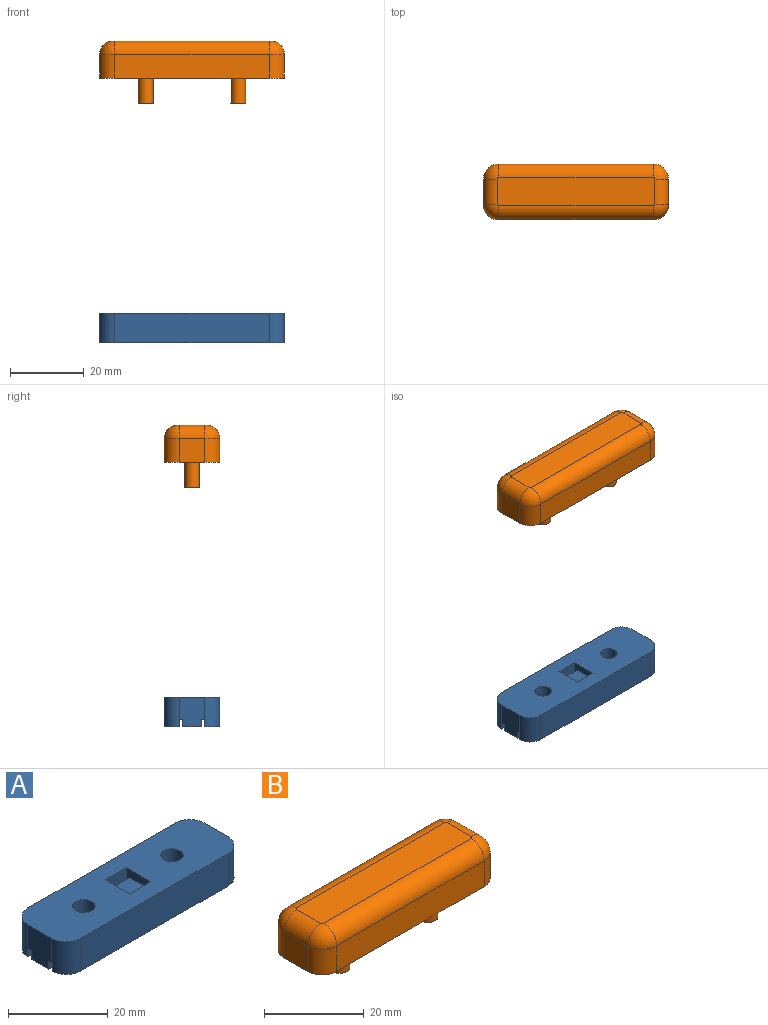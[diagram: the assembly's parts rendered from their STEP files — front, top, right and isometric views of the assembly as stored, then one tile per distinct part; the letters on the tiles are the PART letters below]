
ASSEMBLY  parts=2 mates=1
PART A: 25 faces, bbox 50x15x8 mm
  f0: plane 50x4mm, normal (0,0,-1), area 192.8mm2, adj f6,f7,f21,f22
  f1: plane 50x5mm, normal (0,0,-1), area 218.2mm2, adj f3,f10,f12,f13,f14,f15
  f2: plane 50x4mm, normal (0,0,-1), area 192.8mm2, adj f5,f8,f23,f24
  f3: plane 8x6.82mm, normal (1,0,0), area 50.9mm2, adj f1,f11,f14,f15,f19,f20,f21,f24
  f4: plane 7x6mm, normal (-1,0,0), area 22mm2, adj f7,f8,f11,f14,f15,f16,f19,f20
  f5: plane 41.82x8mm, normal (0,-1,0), area 334.6mm2, adj f2,f11,f23,f24
  f6: plane 41.82x8mm, normal (0,1,0), area 334.6mm2, adj f0,f11,f21,f22
  f7: plane 50x8mm, normal (0,-1,0), area 136mm2, adj f0,f4,f9,f11,f18,f20,f21,f22
  f8: plane 50x8mm, normal (0,1,0), area 136mm2, adj f2,f4,f9,f11,f17,f19,f23,f24
  f9: plane 7x6mm, normal (1,0,0), area 22mm2, adj f7,f8,f11,f14,f15,f16,f17,f18
  f10: plane 8x6.82mm, normal (-1,0,0), area 50.9mm2, adj f1,f11,f14,f15,f17,f18,f22,f23
  f11: plane 50x15mm, normal (0,0,1), area 661.8mm2, adj f3,f4,f5,f6,f7,f8,f9,f10
  f12: cylinder r=2.25mm len=8mm, axis (0,0,-1), area 113.1mm2, adj f1,f11
  f13: cylinder r=2.25mm len=8mm, axis (0,0,-1), area 113.1mm2, adj f1,f11
  f14: plane 50x6mm, normal (0,-1,0), area 124mm2, adj f1,f3,f4,f9,f10,f16,f17,f19
  f15: plane 50x6mm, normal (0,1,0), area 124mm2, adj f1,f3,f4,f9,f10,f16,f18,f20
  f16: plane 6x5mm, normal (0,0,1), area 30mm2, adj f4,f9,f14,f15
  f17: plane 22x1mm, normal (0,0,-1), area 22mm2, adj f8,f9,f10,f14,f23
  f18: plane 22x1mm, normal (0,0,-1), area 22mm2, adj f7,f9,f10,f15,f22
  f19: plane 22x1mm, normal (0,0,-1), area 22mm2, adj f3,f4,f8,f14,f24
  f20: plane 22x1mm, normal (0,0,-1), area 22mm2, adj f3,f4,f7,f15,f21
  f21: cylinder r=4.09mm len=8mm, axis (0,0,1), area 51.2mm2, adj f0,f3,f6,f7,f11,f20
  f22: cylinder r=4.09mm len=8mm, axis (0,0,-1), area 51.2mm2, adj f0,f6,f7,f10,f11,f18
  f23: cylinder r=4.09mm len=8mm, axis (0,0,1), area 51.2mm2, adj f2,f5,f8,f10,f11,f17
  f24: cylinder r=4.09mm len=8mm, axis (0,0,-1), area 51.2mm2, adj f2,f3,f5,f8,f11,f19
PART B: 24 faces, bbox 50x15x17 mm
  f0: plane 42.64x7.64mm, normal (0,0,1), area 325.7mm2, adj f6,f7,f8,f9,f11,f13,f15,f17
  f1: plane 41.82x6.32mm, normal (0,-1,0), area 264.3mm2, adj f5,f6,f14,f16
  f2: plane 6.82x6.32mm, normal (1,0,0), area 43.1mm2, adj f5,f7,f12,f16
  f3: plane 41.82x6.32mm, normal (0,1,0), area 264.3mm2, adj f5,f9,f10,f12
  f4: plane 6.82x6.32mm, normal (-1,0,0), area 43.1mm2, adj f5,f8,f10,f14
  f5: plane 50x15mm, normal (0,0,-1), area 694.6mm2, adj f1,f2,f3,f4,f10,f12,f14,f16
  f6: cylinder r=3.68mm len=41.82mm, axis (-1,0,0), area 241.7mm2, adj f0,f1,f15,f17
  f7: cylinder r=3.68mm len=6.82mm, axis (0,-1,0), area 39.4mm2, adj f0,f2,f13,f17
  f8: cylinder r=3.68mm len=6.82mm, axis (0,1,0), area 39.4mm2, adj f0,f4,f11,f15
  f9: cylinder r=3.68mm len=41.82mm, axis (1,0,0), area 241.7mm2, adj f0,f3,f11,f13
  f10: cylinder r=4.09mm len=6.32mm, axis (0,0,-1), area 40.6mm2, adj f3,f4,f5,f11
  f11: torus R=0.41mm, axis (0,0,1), area 25mm2, adj f0,f8,f9,f10
  f12: cylinder r=4.09mm len=6.32mm, axis (0,0,1), area 40.6mm2, adj f2,f3,f5,f13
  f13: torus R=0.41mm, axis (0,0,1), area 25mm2, adj f0,f7,f9,f12
  f14: cylinder r=4.09mm len=6.32mm, axis (0,0,1), area 40.6mm2, adj f1,f4,f5,f15
  f15: torus R=0.41mm, axis (0,0,1), area 25mm2, adj f0,f6,f8,f14
  f16: cylinder r=4.09mm len=6.32mm, axis (0,0,-1), area 40.6mm2, adj f1,f2,f5,f17
  f17: torus R=0.41mm, axis (0,0,1), area 25mm2, adj f0,f6,f7,f16
  f18: cylinder r=2.25mm len=4.5mm, axis (0,0,-1), area 7.1mm2, adj f5,f19
  f19: cone r=0mm half-angle=59deg, axis (0,0,-1), area 18.6mm2, adj f18
  f20: cylinder r=2mm len=7mm, axis (0,0,1), area 88mm2, adj f5,f21
  f21: plane 4x4mm, normal (0,0,-1), area 12.6mm2, adj f20
  f22: cylinder r=2mm len=7mm, axis (0,0,1), area 88mm2, adj f5,f23
  f23: plane 4x4mm, normal (0,0,-1), area 12.6mm2, adj f22
PLACE A t=(4.55,-4.79,-18.13)mm
PLACE B t=(4.55,-4.79,53.46)mm
MATE slider B.f22 <-> A.f13  axis (0,0,-1) through (17.05,-4.79,46.46)mm
